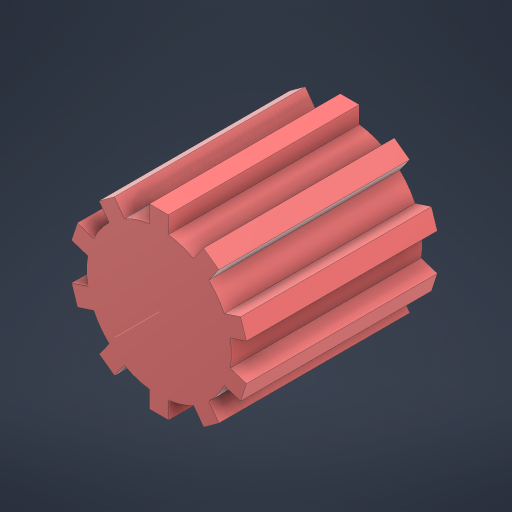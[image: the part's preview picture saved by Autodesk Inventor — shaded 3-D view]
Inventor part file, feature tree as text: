
AUTODESK INVENTOR PART (.ipt)
format: ipt  version: 2024 (Build 280153000, 153)  size: 328,192 bytes
history: native  units: in
note: dims shown in document units (in); Inventor stores cm internally (conversion verified against a paired STEP export)
features: sketch x4, extrude x3, plane x2, projected_geometry x1
ambient origin geometry x8: Origin, YZ Plane, XZ Plane, XY Plane, X Axis, Y Axis, Z Axis, Center Point
bodies: Solid1 (feature_tree)
feature tree (10):
  extrude  "Extrusion1"  Depth=3.937in TaperAngle=360.0deg
  extrude  "Extrusion2"  Depth=0.4331in TaperAngle=0.0deg
  extrude  "Extrusion3"  Depth=0.3543in TaperAngle=0.0deg
  plane  "Work Plane1"
  sketch  "Sketch4"  dims[d14=0.1969in d15=0.4331in d16=1.3386in d17=0.6693in d18=0.0in d24=0.1021in d25=0.1138in]
  plane  "Work Plane2"
  sketch  "Sketch1"  dims[d1=1.1811in d3=3.937in d5=360.0deg]
  sketch  "Sketch2"  dims[d7=1.1417in d8=0.0in d9=0.4331in d10=0.0in]
  projected_geometry  "Projected Loop1"
  sketch  "Sketch3"  dims[d11=0.1969in d12=0.3543in d13=0.0in]
